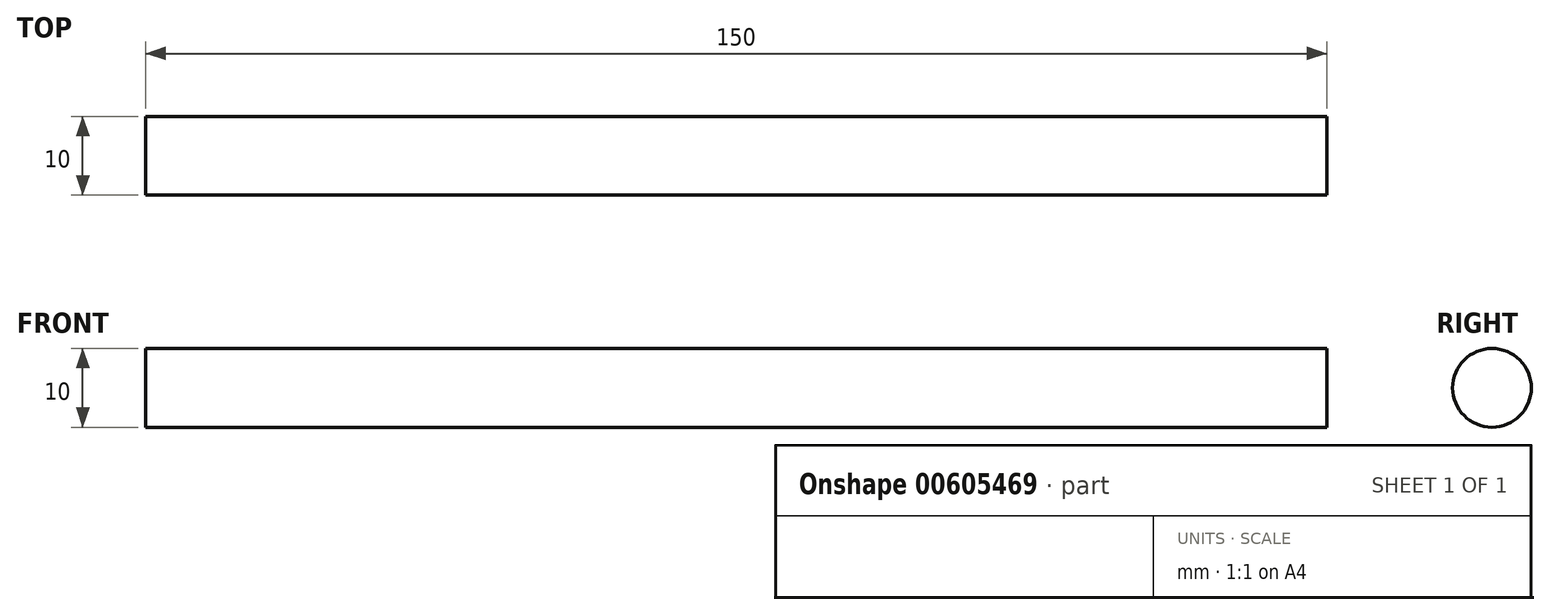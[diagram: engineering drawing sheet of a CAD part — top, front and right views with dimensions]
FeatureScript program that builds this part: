
annotation { "Feature Type Name" : "Feature", "Feature Type Description" : "" }
export const myFeature = defineFeature(function(context is Context, id is Id, definition is map)
    precondition{}
    {
        {
            var Q0;
            Q0=qCreatedBy(makeId("Right.planeOp"),FACE);
            var sketch = newSketch(context, id + "F0", { "sketchPlane" : qUnion([Q0])});
            skCircle(sketch, "E0", {"center": v(0, 0) * mm, "radius": 5 * mm});
            skSolve(sketch);
        }
        {
            var Q0;
            Q0=makeQuery(id+"F0.imprint","IMPRINT",FACE,{"disambiguationData":[TD([[makeQuery(id+"F0.imprint","IMPRINT",EDGE,{"derivedFrom":sQuery(id+"F0.wireOp",EDGE,"E0")}),1.0]])]});
            extrude(context, id + "F1", {"entities" : qUnion([Q0]), "depth" : 150 * mm, "offsetDistance" : 25 * mm});
        }
    });
